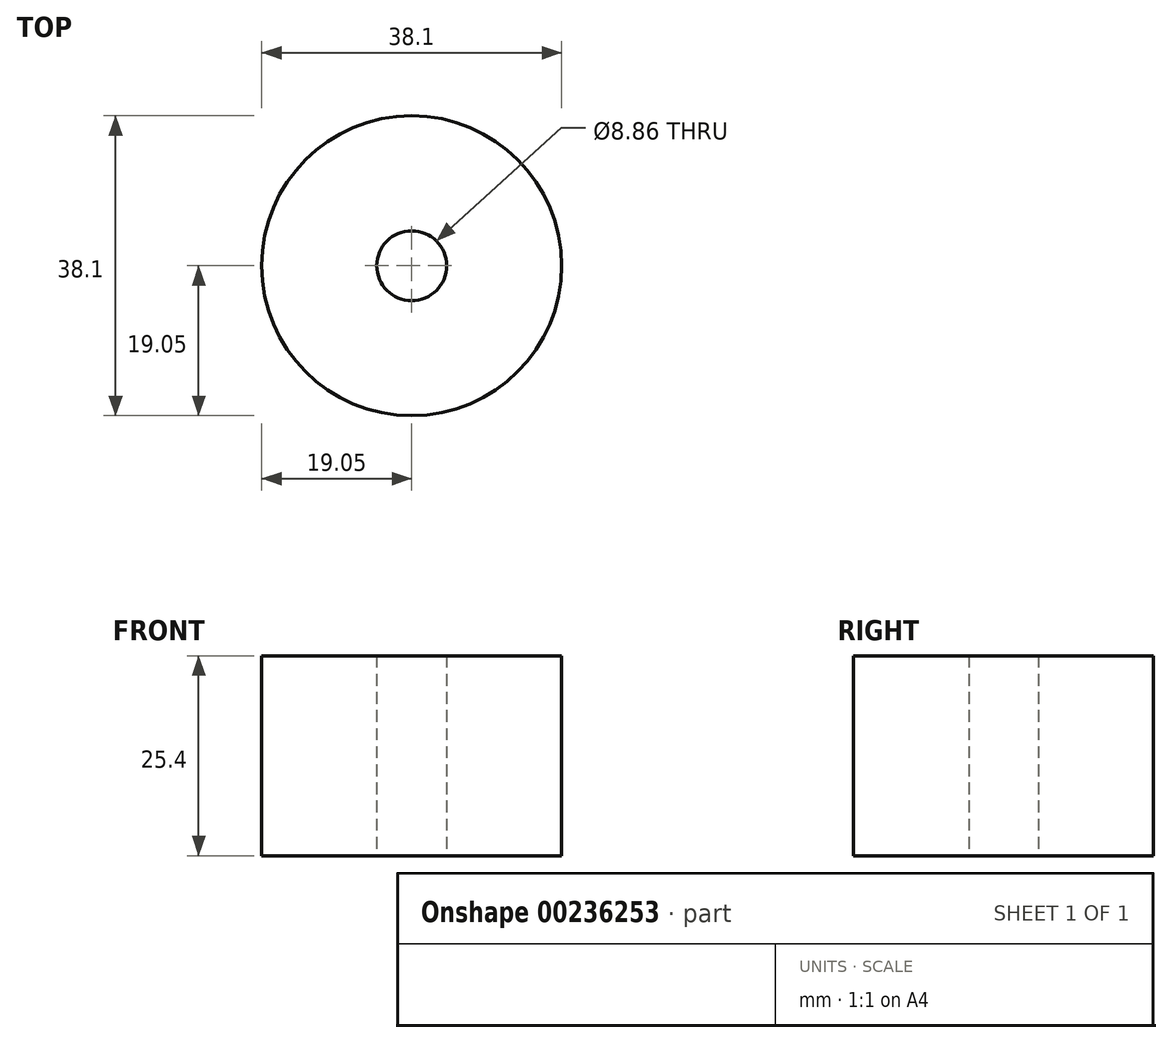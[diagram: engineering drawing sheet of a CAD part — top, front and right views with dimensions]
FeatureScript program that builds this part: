
annotation { "Feature Type Name" : "Feature", "Feature Type Description" : "" }
export const myFeature = defineFeature(function(context is Context, id is Id, definition is map)
    precondition{}
    {
        {
            var Q0;
            Q0=qCreatedBy(makeId("Top.planeOp"),FACE);
            var sketch = newSketch(context, id + "F0", { "sketchPlane" : qUnion([Q0])});
            skCircle(sketch, "E0", {"center": v(0, 0) * mm, "radius": 19.05 * mm});
            skSolve(sketch);
        }
        {
            var Q0;
            Q0=makeQuery(id+"F0.imprint","IMPRINT",FACE,{"disambiguationData":[TD([[makeQuery(id+"F0.imprint","IMPRINT",EDGE,{"derivedFrom":sQuery(id+"F0.wireOp",EDGE,"E0")}),1.0]])]});
            extrude(context, id + "F1", {"entities" : qUnion([Q0]), "endBound" : BoundingType.SYMMETRIC, "depth" : 25.4 * mm});
        }
        {
            var Q0;
            Q0=qCreatedBy(makeId("Top.planeOp"),FACE);
            var sketch = newSketch(context, id + "F2", { "sketchPlane" : qUnion([Q0])});
            skCircle(sketch, "E1", {"center": v(0, 0) * mm, "radius": 4.43 * mm});
            skSolve(sketch);
        }
        {
            var Q0;
            Q0 = qSketchRegion(id + "F2", true);
            extrude(context, id + "F3", {"entities" : qUnion([Q0]), "operationType" : NewBodyOperationType.REMOVE, "endBound" : BoundingType.SYMMETRIC, "depth" : 35.05 * mm});
        }
    });
